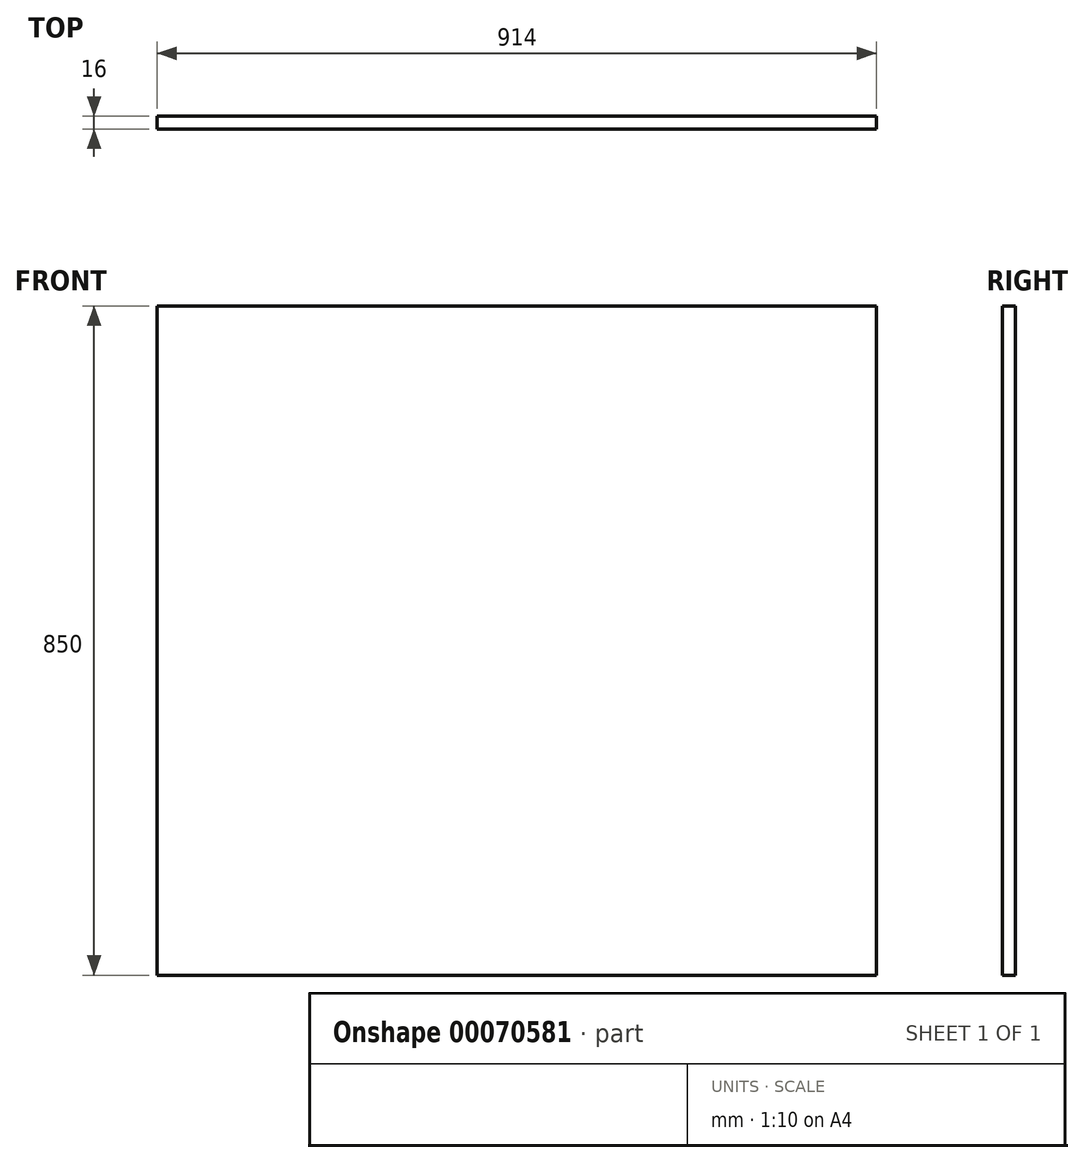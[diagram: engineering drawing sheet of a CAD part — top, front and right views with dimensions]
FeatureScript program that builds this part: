
annotation { "Feature Type Name" : "Feature", "Feature Type Description" : "" }
export const myFeature = defineFeature(function(context is Context, id is Id, definition is map)
    precondition{}
    {
        {
            var Q0;
            Q0=qCreatedBy(makeId("Front.planeOp"),FACE);
            var sketch = newSketch(context, id + "F0", { "sketchPlane" : qUnion([Q0])});
            skLineSegment(sketch, "E0.bottom", {"start": v(0, 0) * mm, "end": v(914, 0) * mm});
            skLineSegment(sketch, "E0.top", {"start": v(0, 850) * mm, "end": v(914, 850) * mm});
            skLineSegment(sketch, "E0.left", {"start": v(0, 0) * mm, "end": v(0, 850) * mm});
            skLineSegment(sketch, "E0.right", {"start": v(914, 0) * mm, "end": v(914, 850) * mm});
            skSolve(sketch);
        }
        {
            var Q0;
            Q0=makeQuery(id+"F0.imprint","IMPRINT",FACE,{"disambiguationData":[TD([[makeQuery(id+"F0.imprint","IMPRINT",EDGE,{"derivedFrom":sQuery(id+"F0.wireOp",EDGE,"E0.bottom")}),1.0]])]});
            extrude(context, id + "F1", {"entities" : qUnion([Q0]), "depth" : 16 * mm});
        }
    });
